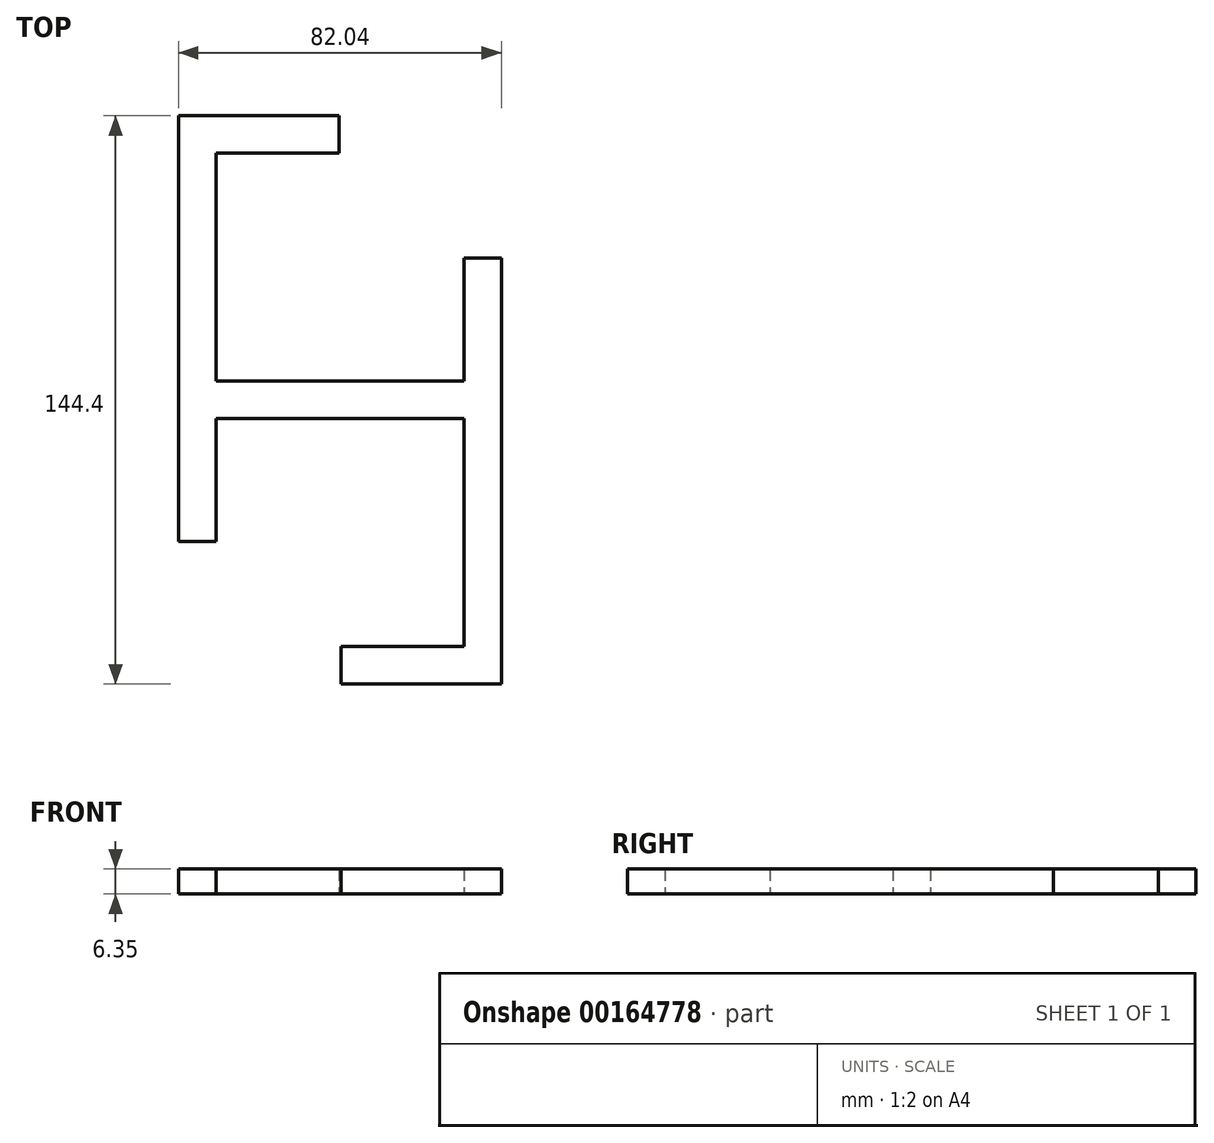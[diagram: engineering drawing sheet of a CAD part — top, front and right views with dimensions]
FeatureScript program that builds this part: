
annotation { "Feature Type Name" : "Feature", "Feature Type Description" : "" }
export const myFeature = defineFeature(function(context is Context, id is Id, definition is map)
    precondition{}
    {
        {
            var Q0;
            Q0=qCreatedBy(makeId("Top.planeOp"),FACE);
            var sketch = newSketch(context, id + "F0", { "sketchPlane" : qUnion([Q0])});
            skLineSegment(sketch, "E0", {"start": v(0, 0) * mm, "end": v(0, 57.91) * mm, "construction": true});
            skLineSegment(sketch, "E1", {"start": v(0, 57.91) * mm, "end": v(-0.25, 57.91) * mm, "construction": true});
            skLineSegment(sketch, "E2.bottom", {"start": v(-0.25, 57.91) * mm, "end": v(-31.5, 57.91) * mm});
            skLineSegment(sketch, "E2.top", {"start": v(-0.25, 67.44) * mm, "end": v(-41.02, 67.44) * mm});
            skLineSegment(sketch, "E2.left", {"start": v(-0.25, 57.91) * mm, "end": v(-0.25, 67.44) * mm});
            skLineSegment(sketch, "E3.top", {"start": v(-31.5, 0) * mm, "end": v(31.5, 0) * mm});
            skLineSegment(sketch, "E3.left", {"start": v(-31.5, 57.91) * mm, "end": v(-31.5, 0) * mm});
            skLineSegment(sketch, "E4", {"start": v(0, 0) * mm, "end": v(0, -9.53) * mm, "construction": true});
            skLineSegment(sketch, "E5", {"start": v(31.5, 0) * mm, "end": v(31.5, 31.24) * mm});
            skLineSegment(sketch, "E6", {"start": v(31.5, 31.24) * mm, "end": v(41.02, 31.24) * mm});
            skLineSegment(sketch, "E7", {"start": v(41.02, 31.24) * mm, "end": v(41.02, -76.96) * mm});
            skLineSegment(sketch, "E8", {"start": v(41.02, -76.96) * mm, "end": v(0.25, -76.96) * mm});
            skLineSegment(sketch, "E9", {"start": v(0.25, -76.96) * mm, "end": v(0.25, -67.44) * mm});
            skLineSegment(sketch, "E10", {"start": v(0.25, -67.44) * mm, "end": v(31.5, -67.44) * mm});
            skLineSegment(sketch, "E11", {"start": v(31.5, -9.52) * mm, "end": v(-31.5, -9.53) * mm});
            skLineSegment(sketch, "E12", {"start": v(-41.02, -40.77) * mm, "end": v(-41.02, 67.44) * mm});
            skLineSegment(sketch, "E13", {"start": v(-31.5, -9.53) * mm, "end": v(-31.5, -40.77) * mm});
            skLineSegment(sketch, "E14", {"start": v(-31.5, -40.77) * mm, "end": v(-41.02, -40.77) * mm});
            skLineSegment(sketch, "E15", {"start": v(31.5, -9.53) * mm, "end": v(31.5, -67.44) * mm});
            skLineSegment(sketch, "E16", {"start": v(0, -9.53) * mm, "end": v(0, -67.44) * mm, "construction": true});
            skLineSegment(sketch, "E17", {"start": v(0, -67.44) * mm, "end": v(0.25, -67.44) * mm, "construction": true});
            skSolve(sketch);
        }
        {
            var Q0;
            Q0 = qSketchRegion(id + "F0", true);
            extrude(context, id + "F1", {"entities" : qUnion([Q0]), "depth" : 6.35 * mm});
        }
    });
